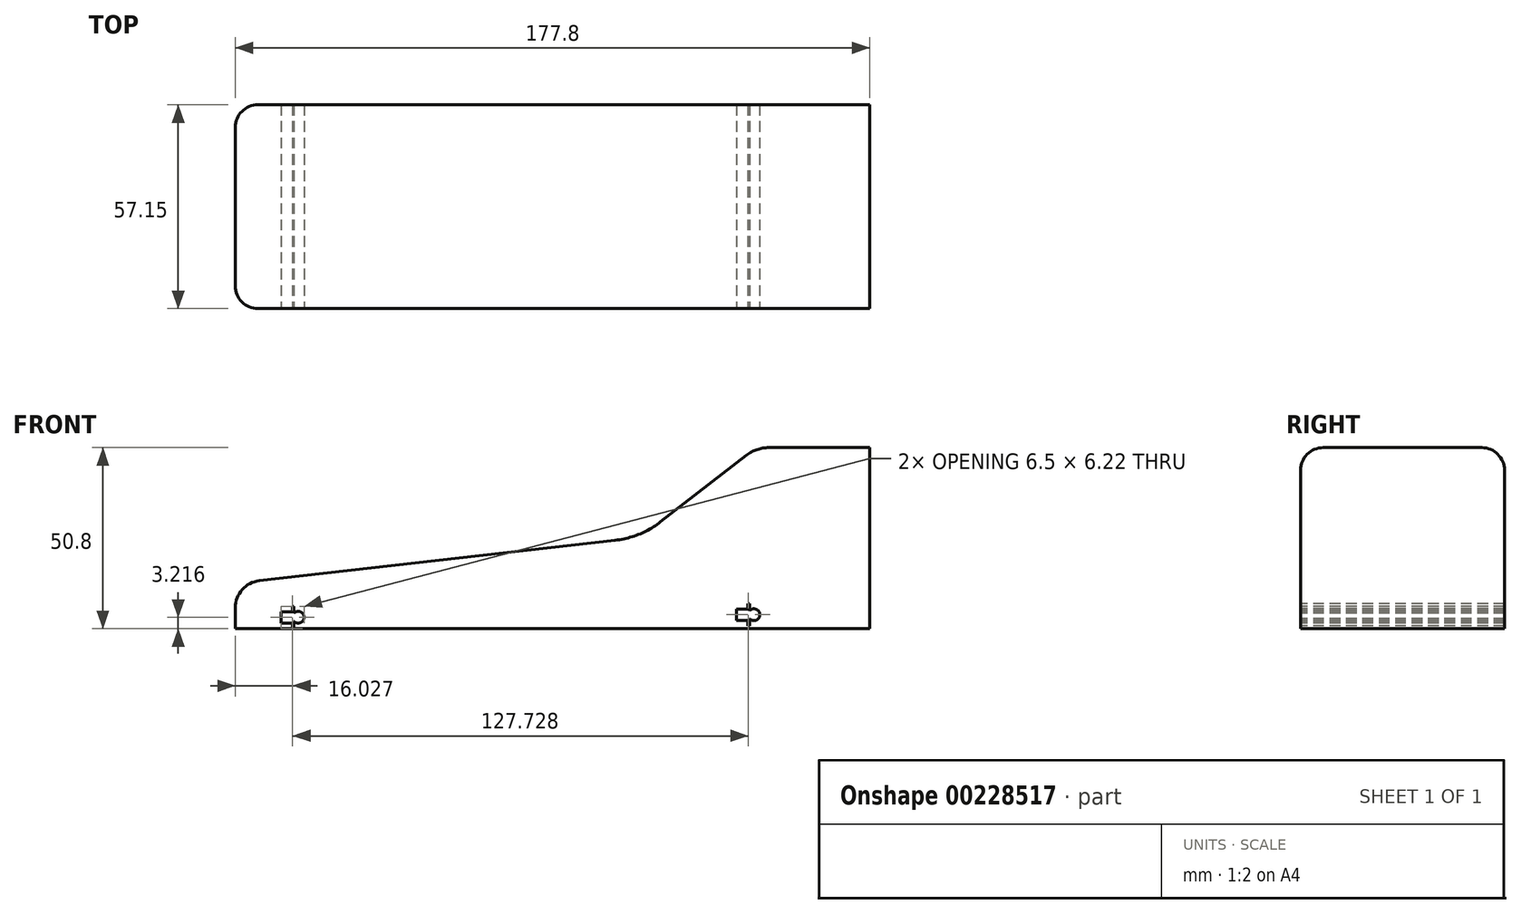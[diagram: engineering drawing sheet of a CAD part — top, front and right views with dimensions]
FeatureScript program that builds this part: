
annotation { "Feature Type Name" : "Feature", "Feature Type Description" : "" }
export const myFeature = defineFeature(function(context is Context, id is Id, definition is map)
    precondition{}
    {
        {
            var Q0;
            Q0=qCreatedBy(makeId("Front.planeOp"),FACE);
            var sketch = newSketch(context, id + "F0", { "sketchPlane" : qUnion([Q0])});
            skLineSegment(sketch, "E0", {"start": v(0, 0) * mm, "end": v(88.9, 0) * mm});
            skLineSegment(sketch, "E1", {"start": v(88.9, 0) * mm, "end": v(88.9, 50.8) * mm});
            skLineSegment(sketch, "E2", {"start": v(88.9, 50.8) * mm, "end": v(57.15, 50.8) * mm});
            skLineSegment(sketch, "E3", {"start": v(0, 0) * mm, "end": v(-88.9, 0) * mm});
            skLineSegment(sketch, "E4", {"start": v(-88.9, 0) * mm, "end": v(-88.9, 12.7) * mm});
            skLineSegment(sketch, "E5", {"start": v(-88.9, 12.7) * mm, "end": v(24.67, 25.62) * mm});
            skLineSegment(sketch, "E6", {"start": v(24.67, 25.62) * mm, "end": v(57.15, 50.8) * mm});
            skSolve(sketch);
        }
        {
            var Q0;
            Q0=makeQuery(id+"F0.imprint","IMPRINT",FACE,{"disambiguationData":[TD([[makeQuery(id+"F0.imprint","IMPRINT",EDGE,{"derivedFrom":sQuery(id+"F0.wireOp",EDGE,"E0")}),1.0]])]});
            extrude(context, id + "F1", {"entities" : qUnion([Q0]), "depth" : 57.15 * mm});
        }
        {
            var Q0;
            Q0=makeQuery(id+"F1.opExtrude","SWEPT_EDGE",EDGE,{"disambiguationData":[OSD([sQuery(id+"F0.wireOp",EDGE,"E4"),sQuery(id+"F0.wireOp",EDGE,"E5")])]});
            fillet(context, id + "F2", {"entities" : qUnion([Q0]), "radius" : 7.62 * mm, "tangentPropagation" : true, "allowEdgeOverflow" : false});
        }
        {
            var Q0;
            Q0=makeQuery(id+"F1.opExtrude","SWEPT_EDGE",EDGE,{"disambiguationData":[OSD([sQuery(id+"F0.wireOp",EDGE,"E2"),sQuery(id+"F0.wireOp",EDGE,"E6")])]});
            fillet(context, id + "F3", {"entities" : qUnion([Q0]), "radius" : 10.16 * mm, "tangentPropagation" : true, "allowEdgeOverflow" : false});
        }
        {
            var Q0;
            Q0=makeQuery(id+"F1.opExtrude","SWEPT_EDGE",EDGE,{"disambiguationData":[OSD([sQuery(id+"F0.wireOp",EDGE,"E5"),sQuery(id+"F0.wireOp",EDGE,"E6")])]});
            fillet(context, id + "F4", {"entities" : qUnion([Q0]), "radius" : 25.4 * mm, "tangentPropagation" : true, "rho" : 0.5, "crossSection" : FilletCrossSection.CONIC, "allowEdgeOverflow" : false});
        }
        {
            var Q0;
            Q0=makeQuery(id+"F1.opExtrude","CAP_EDGE",EDGE,{"disambiguationData":[OSD([sQuery(id+"F0.wireOp",EDGE,"E2")])],"isStart":true});
            fillet(context, id + "F5", {"entities" : qUnion([Q0]), "radius" : 6.35 * mm, "tangentPropagation" : true, "allowEdgeOverflow" : false});
        }
        {
            var Q0;
            Q0=makeQuery(id+"F1.opExtrude","CAP_EDGE",EDGE,{"disambiguationData":[OSD([sQuery(id+"F0.wireOp",EDGE,"E5")])],"isStart":false});
            fillet(context, id + "F6", {"entities" : qUnion([Q0]), "radius" : 6.35 * mm, "tangentPropagation" : true, "allowEdgeOverflow" : false});
        }
        {
            var Q0;
            Q0=makeQuery(id+"F1.opExtrude","CAP_FACE",FACE,{"disambiguationData":[OSD([sQuery(id+"F0.wireOp",EDGE,"E0"),sQuery(id+"F0.wireOp",EDGE,"E1"),sQuery(id+"F0.wireOp",EDGE,"E2"),sQuery(id+"F0.wireOp",EDGE,"E3"),sQuery(id+"F0.wireOp",EDGE,"E4"),sQuery(id+"F0.wireOp",EDGE,"E5"),sQuery(id+"F0.wireOp",EDGE,"E6")])],"isStart":false});
            var sketch = newSketch(context, id + "F7", { "sketchPlane" : qUnion([Q0])});
            skLineSegment(sketch, "E7", {"start": v(0, 0) * mm, "end": v(23.01, 0) * mm});
            skLineSegment(sketch, "E8", {"start": v(23.01, 0) * mm, "end": v(23.01, 17.35) * mm});
            skLineSegment(sketch, "E9", {"start": v(23.01, 17.35) * mm, "end": v(54.76, 17.35) * mm});
            skLineSegment(sketch, "E10", {"start": v(54.76, 17.35) * mm, "end": v(54.76, 0) * mm});
            skLineSegment(sketch, "E11", {"start": v(54.76, 0) * mm, "end": v(-72.24, 0) * mm});
            skSolve(sketch);
        }
        {
            var Q0;
            {var subQ12=sQuery(id+"F7.wireOp",EDGE,"E8");Q0=makeQuery(id+"F7.imprint","IMPRINT",FACE,{"disambiguationData":[TD([[makeQuery(id+"F7.imprint","IMPRINT",EDGE,{"derivedFrom":subQ12}),1.0]])]});}
            var sketch = newSketch(context, id + "F8", { "sketchPlane" : qUnion([Q0])});
            skLineSegment(sketch, "E12", {"start": v(-76.12, 1.63) * mm, "end": v(-76.12, 4.8) * mm});
            skLineSegment(sketch, "E13", {"start": v(-76.12, 4.8) * mm, "end": v(-72.95, 4.8) * mm});
            skLineSegment(sketch, "E14", {"start": v(-72.95, 4.8) * mm, "end": v(-72.95, 6.33) * mm});
            skLineSegment(sketch, "E15", {"start": v(-72.95, 6.33) * mm, "end": v(-72.51, 6.33) * mm});
            skLineSegment(sketch, "E16", {"start": v(-72.51, 6.33) * mm, "end": v(-72.51, 4.33) * mm});
            skLineSegment(sketch, "E17", {"start": v(-72.51, 0.1) * mm, "end": v(-72.95, 0.1) * mm});
            skLineSegment(sketch, "E18", {"start": v(-72.95, 0.1) * mm, "end": v(-72.95, 1.63) * mm});
            skLineSegment(sketch, "E19", {"start": v(-72.95, 1.63) * mm, "end": v(-76.12, 1.63) * mm});
            skCircle(sketch, "E20", {"center": v(-71.29, 3.22) * mm, "radius": 1.66 * mm});
            skPoint(sketch, "E20.first.point", {"position": v(-72.95, 3.22) * mm});
            skPoint(sketch, "E20.second.point", {"position": v(-69.66, 3.54) * mm});
            skPoint(sketch, "E20.third.point", {"position": v(-72.51, 2.1) * mm});
            skLineSegment(sketch, "E21.trimOffspring", {"start": v(-72.51, 2.1) * mm, "end": v(-72.51, 0.1) * mm});
            skSolve(sketch);
        }
        {
            var Q0;
            Q0 = qSketchRegion(id + "F8", true);
            extrude(context, id + "F9", {"entities" : qUnion([Q0]), "operationType" : NewBodyOperationType.REMOVE, "oppositeDirection" : true, "depth" : 57.15 * mm});
        }
        {
            var Q0;
            {var subQ12=sQuery(id+"F7.wireOp",EDGE,"E8");Q0=makeQuery(id+"F7.imprint","IMPRINT",FACE,{"disambiguationData":[TD([[makeQuery(id+"F7.imprint","IMPRINT",EDGE,{"derivedFrom":subQ12}),1.0]])]});}
            var sketch = newSketch(context, id + "F10", { "sketchPlane" : qUnion([Q0])});
            skLineSegment(sketch, "E22", {"start": v(51.6, 2.35) * mm, "end": v(51.6, 5.52) * mm});
            skLineSegment(sketch, "E23", {"start": v(51.6, 5.52) * mm, "end": v(54.78, 5.52) * mm});
            skLineSegment(sketch, "E24", {"start": v(54.78, 5.52) * mm, "end": v(54.78, 7.05) * mm});
            skLineSegment(sketch, "E25", {"start": v(54.78, 7.05) * mm, "end": v(55.21, 7.05) * mm});
            skLineSegment(sketch, "E26", {"start": v(55.21, 7.05) * mm, "end": v(55.21, 5.05) * mm});
            skLineSegment(sketch, "E27", {"start": v(55.21, 0.83) * mm, "end": v(54.78, 0.83) * mm});
            skLineSegment(sketch, "E28", {"start": v(54.78, 0.83) * mm, "end": v(54.78, 2.35) * mm});
            skLineSegment(sketch, "E29", {"start": v(54.78, 2.35) * mm, "end": v(51.6, 2.35) * mm});
            skCircle(sketch, "E30", {"center": v(56.44, 3.94) * mm, "radius": 1.66 * mm});
            skPoint(sketch, "E30.first.point", {"position": v(54.78, 3.94) * mm});
            skPoint(sketch, "E30.second.point", {"position": v(58.07, 4.26) * mm});
            skPoint(sketch, "E30.third.point", {"position": v(55.21, 2.82) * mm});
            skLineSegment(sketch, "E31.trimOffspring", {"start": v(55.21, 2.82) * mm, "end": v(55.21, 0.83) * mm});
            skSolve(sketch);
        }
        {
            var Q0;
            {var subQ0=sQuery(id+"F10.wireOp",EDGE,"E22");Q0=makeQuery(id+"F10.imprint","IMPRINT",FACE,{"disambiguationData":[TD([[makeQuery(id+"F10.imprint","IMPRINT",EDGE,{"derivedFrom":subQ0}),-1.0]])]});}
            var Q1;
            {var subQ0=sQuery(id+"F10.wireOp",EDGE,"E30");var subQ1=makeQuery(id+"F10.imprint","INTERSECT",VERTEX,{"derivedFrom":[sQuery(id+"F10.wireOp",EDGE,"E26"),subQ0]});Q1=makeQuery(id+"F10.imprint","IMPRINT",FACE,{"disambiguationData":[TD([[makeQuery(id+"F10.imprint","IMPRINT",EDGE,{"disambiguationData":[TD([[subQ1,-1.0]])],"derivedFrom":subQ0}),1.0]])]});}
            var Q2;
            {var subQ2=sQuery(id+"F10.wireOp",EDGE,"E24");Q2=makeQuery(id+"F10.imprint","IMPRINT",FACE,{"disambiguationData":[TD([[makeQuery(id+"F10.imprint","IMPRINT",EDGE,{"derivedFrom":subQ2}),-1.0]])]});}
            extrude(context, id + "F11", {"entities" : qUnion([Q0, Q1, Q2]), "operationType" : NewBodyOperationType.REMOVE, "oppositeDirection" : true, "depth" : 57.15 * mm});
        }
    });
